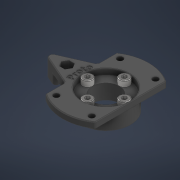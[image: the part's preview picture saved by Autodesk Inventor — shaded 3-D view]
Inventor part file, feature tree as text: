
AUTODESK INVENTOR PART (.ipt)
format: ipt  version: 2022 (Build 260153070, 153G)  size: 595,968 bytes
history: native  units: mm
features: other x6, extrude x1, sketch x1
ambient origin geometry x8: Origin, YZ Plane, XZ Plane, XY Plane, X Axis, Y Axis, Z Axis, Center Point
bodies: Solid1 (feature_tree)
feature tree (8):
  other  "Plate_link.iam"
  other  "Final_rotary_plate.ipt:1"
  other  "DIN 912 - replaced by DIN EN ISO 4762 M4 x 16:3"
  other  "DIN 912 - replaced by DIN EN ISO 4762 M4 x 16:1"
  other  "DIN 912 - replaced by DIN EN ISO 4762 M4 x 16:2"
  other  "DIN 912 - replaced by DIN EN ISO 4762 M4 x 16:4"
  extrude  "Extrusion1"  TaperAngle=0.0deg  [1 undecoded]
  sketch  "Sketch1"  dims[d0=10.0mm d1=0.0mm d2=0.0mm]
note: 1 required parameter value undecoded (feature->parameter linkage not recoverable at this tier; creation-order binding heuristic only, values carry confidence <= 0.55)
